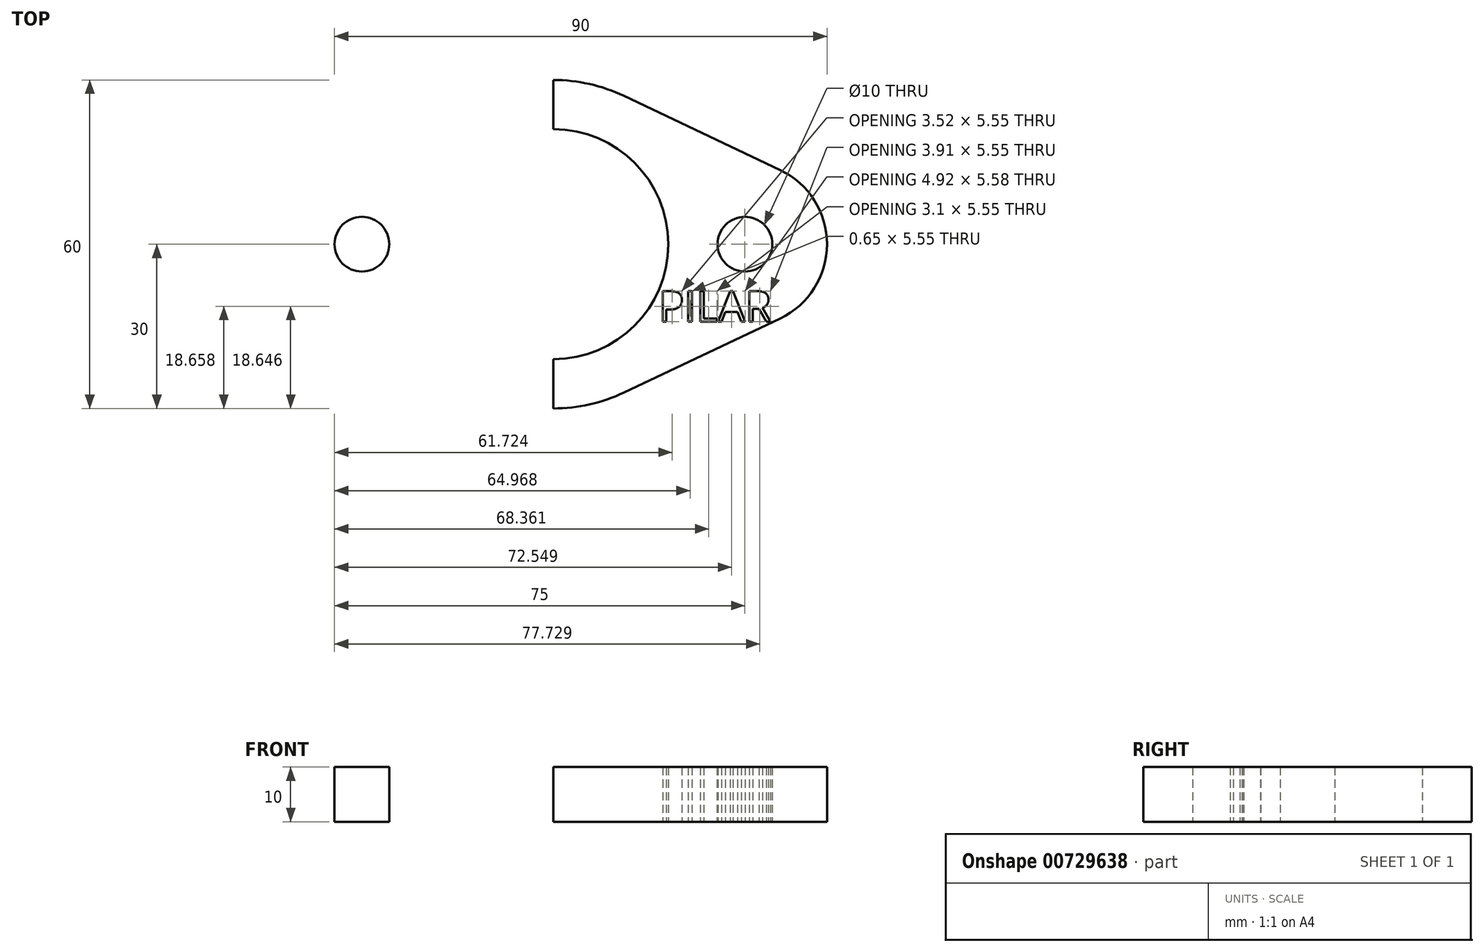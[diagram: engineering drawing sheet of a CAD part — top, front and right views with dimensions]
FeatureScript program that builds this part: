
annotation { "Feature Type Name" : "Feature", "Feature Type Description" : "" }
export const myFeature = defineFeature(function(context is Context, id is Id, definition is map)
    precondition{}
    {
        {
            var Q0;
            Q0=qCreatedBy(makeId("Top.planeOp"),FACE);
            var sketch = newSketch(context, id + "F0", { "sketchPlane" : qUnion([Q0])});
            skArc(sketch, "E0", {"start": v(0, -21) * mm, "mid": v(21, 0) * mm, "end": v(0, 21) * mm});
            skCircle(sketch, "E1", {"center": v(35, 0) * mm, "radius": 5 * mm});
            skLineSegment(sketch, "E2", {"start": v(0, 0) * mm, "end": v(35, 0) * mm, "construction": true});
            skArc(sketch, "E3", {"start": v(12.86, 27.1) * mm, "mid": v(6.59, 29.27) * mm, "end": v(0, 30) * mm});
            skLineSegment(sketch, "E4", {"start": v(12.86, 27.1) * mm, "end": v(41.43, 13.55) * mm});
            skLineSegment(sketch, "E5", {"start": v(12.86, -27.1) * mm, "end": v(41.43, -13.55) * mm});
            skArc(sketch, "E6.trimOffspring", {"start": v(41.43, -13.55) * mm, "mid": v(50, 0) * mm, "end": v(41.43, 13.55) * mm});
            skArc(sketch, "E7.trimOffspring", {"start": v(0, -30) * mm, "mid": v(6.59, -29.27) * mm, "end": v(12.86, -27.1) * mm});
            skLineSegment(sketch, "E8", {"start": v(0, 43.77) * mm, "end": v(0, -47.45) * mm});
            skLineSegment(sketch, "E9", {"start": v(0, -47.45) * mm, "end": v(0, 43.77) * mm, "construction": true});
            skPoint(sketch, "E10.end.orphan", {"position": v(-35, 0) * mm});
            skPoint(sketch, "E11.orphan", {"position": v(0, 50.56) * mm});
            skCircle(sketch, "E12.MirrorC", {"center": v(-35, 0) * mm, "radius": 5 * mm});
            skArc(sketch, "E13.MirrorCS", {"start": v(0, -30) * mm, "mid": v(-6.59, -29.27) * mm, "end": v(-12.86, -27.1) * mm});
            skLineSegment(sketch, "E14.MirrorCS", {"start": v(-12.86, -27.1) * mm, "end": v(-41.43, -13.55) * mm});
            skArc(sketch, "E15.MirrorCS", {"start": v(-41.43, -13.55) * mm, "mid": v(-50, 0) * mm, "end": v(-41.43, 13.55) * mm});
            skLineSegment(sketch, "E16.MirrorCS", {"start": v(-12.86, 27.1) * mm, "end": v(-41.43, 13.55) * mm});
            skArc(sketch, "E17.MirrorCS", {"start": v(-12.86, 27.1) * mm, "mid": v(-6.59, 29.27) * mm, "end": v(0, 30) * mm});
            skArc(sketch, "E18.MirrorCS", {"start": v(0, -21) * mm, "mid": v(-21, 0) * mm, "end": v(0, 21) * mm});
            skLineSegment(sketch, "E19.MirrorCS", {"start": v(0, 0) * mm, "end": v(-35, 0) * mm, "construction": true});
            skText(sketch, "E20", { "text": "PILAR\n", "fontName": "OpenSans-Regular.ttf"});
            skText(sketch, "E21", { "text": "PILAR\n", "fontName": "OpenSans-Regular.ttf"});
            const initialGuessF0  = {"E20": [0.0192, -0.01413, 1, 0, 0.0056], "E21": [-0.04062, -0.01224, 1, 0, 0.00545]};
            skSetInitialGuess(sketch, initialGuessF0);
            skSolve(sketch);
        }
        {
            var Q0;
            Q0=makeQuery(id+"F0.imprint","IMPRINT",FACE,{"disambiguationData":[TD([[makeQuery(id+"F0.imprint","IMPRINT",EDGE,{"derivedFrom":sQuery(id+"F0.wireOp",EDGE,"E0")}),-1.0]])]});
            var Q1;
            Q1=makeQuery(id+"F0.imprint","IMPRINT",FACE,{"disambiguationData":[TD([[makeQuery(id+"F0.imprint","IMPRINT",EDGE,{"derivedFrom":sQuery(id+"F0.wireOp",EDGE,"E12.MirrorC")}),1.0]])]});
            extrude(context, id + "F1", {"entities" : qUnion([Q0, Q1]), "depth" : 10 * mm, "offsetDistance" : 25 * mm});
        }
    });
